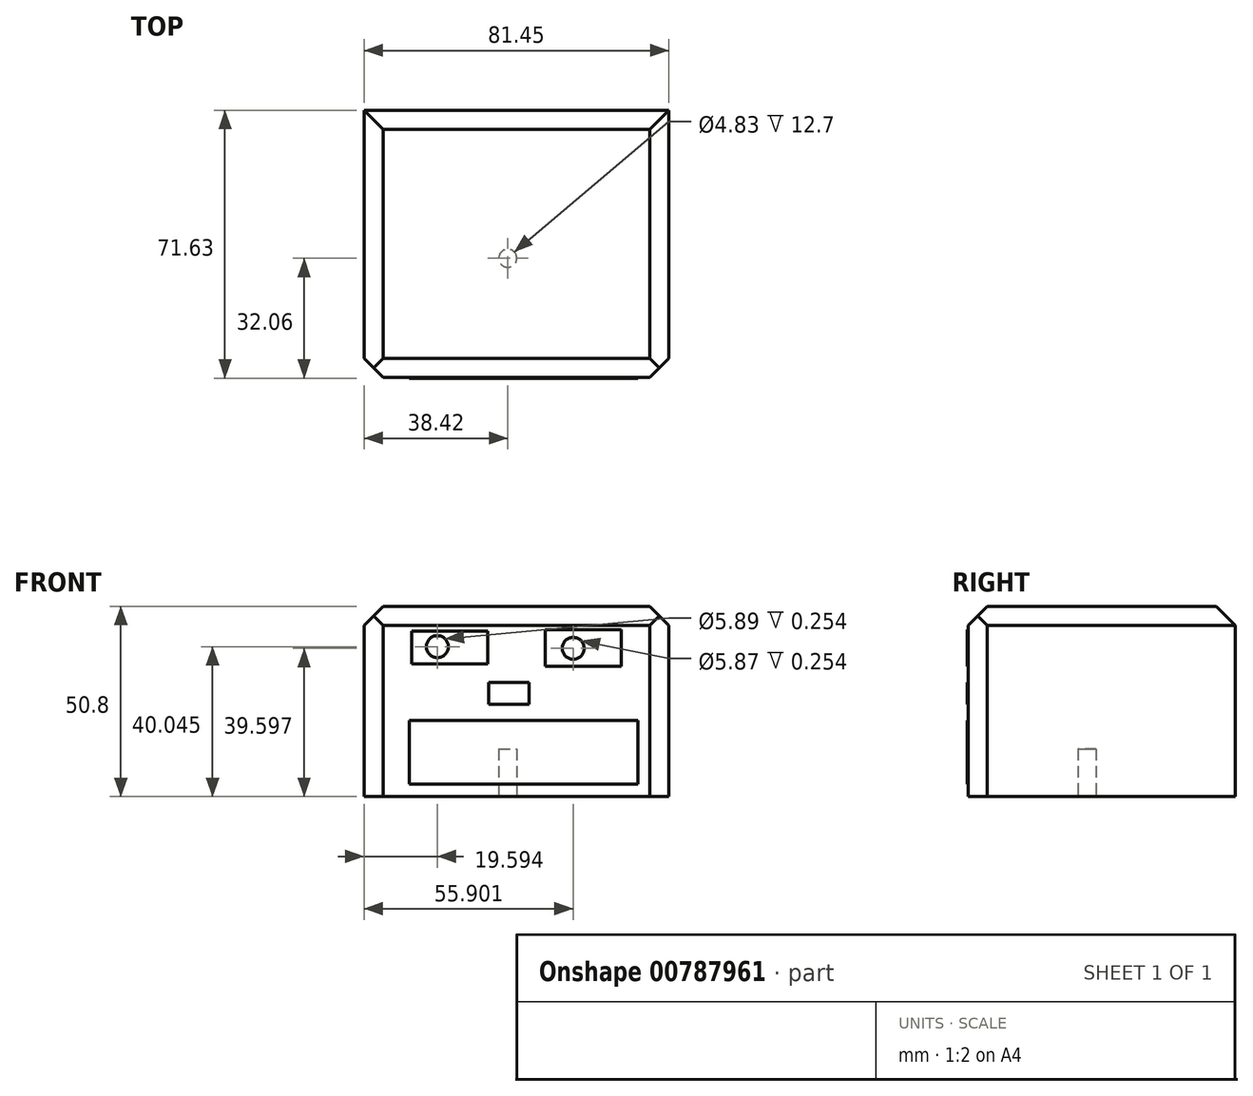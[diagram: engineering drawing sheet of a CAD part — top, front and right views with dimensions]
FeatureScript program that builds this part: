
annotation { "Feature Type Name" : "Feature", "Feature Type Description" : "" }
export const myFeature = defineFeature(function(context is Context, id is Id, definition is map)
    precondition{}
    {
        {
            var Q0;
            Q0=qCreatedBy(makeId("Top.planeOp"),FACE);
            var sketch = newSketch(context, id + "F0", { "sketchPlane" : qUnion([Q0])});
            skLineSegment(sketch, "E0.bottom", {"start": v(-38.42, 39.57) * mm, "end": v(43.03, 39.57) * mm});
            skLineSegment(sketch, "E0.top", {"start": v(-38.42, -31.8) * mm, "end": v(43.03, -31.8) * mm});
            skLineSegment(sketch, "E0.left", {"start": v(-38.42, 39.57) * mm, "end": v(-38.42, -31.8) * mm});
            skLineSegment(sketch, "E0.right", {"start": v(43.03, 39.57) * mm, "end": v(43.03, -31.8) * mm});
            skSolve(sketch);
        }
        {
            var Q0;
            Q0 = qSketchRegion(id + "F0", true);
            extrude(context, id + "F1", {"entities" : qUnion([Q0]), "depth" : 50.8 * mm, "offsetDistance" : 25.4 * mm});
        }
        {
            var Q0;
            Q0=makeQuery(id+"F1.opExtrude","SWEPT_FACE",FACE,{"disambiguationData":[OSD([sQuery(id+"F0.wireOp",EDGE,"E0.top")])]});
            var sketch = newSketch(context, id + "F2", { "sketchPlane" : qUnion([Q0])});
            skLineSegment(sketch, "E1.bottom", {"start": v(-25.72, 44.23) * mm, "end": v(-5.4, 44.23) * mm});
            skLineSegment(sketch, "E1.top", {"start": v(-25.72, 35.41) * mm, "end": v(-5.4, 35.41) * mm});
            skLineSegment(sketch, "E1.left", {"start": v(-25.72, 44.23) * mm, "end": v(-25.72, 35.41) * mm});
            skLineSegment(sketch, "E1.right", {"start": v(-5.4, 44.23) * mm, "end": v(-5.4, 35.41) * mm});
            skLineSegment(sketch, "E2.bottom", {"start": v(10, 44.52) * mm, "end": v(30.33, 44.52) * mm});
            skLineSegment(sketch, "E2.top", {"start": v(10, 34.81) * mm, "end": v(30.33, 34.81) * mm});
            skLineSegment(sketch, "E2.left", {"start": v(10, 44.52) * mm, "end": v(10, 34.81) * mm});
            skLineSegment(sketch, "E2.right", {"start": v(30.33, 44.52) * mm, "end": v(30.33, 34.81) * mm});
            skLineSegment(sketch, "E3.bottom", {"start": v(-5.08, 30.48) * mm, "end": v(5.68, 30.48) * mm});
            skLineSegment(sketch, "E3.top", {"start": v(-5.08, 24.65) * mm, "end": v(5.68, 24.65) * mm});
            skLineSegment(sketch, "E3.left", {"start": v(-5.08, 30.48) * mm, "end": v(-5.08, 24.65) * mm});
            skLineSegment(sketch, "E3.right", {"start": v(5.68, 30.48) * mm, "end": v(5.68, 24.65) * mm});
            skLineSegment(sketch, "E4.bottom", {"start": v(-26.3, 20.32) * mm, "end": v(34.81, 20.32) * mm});
            skLineSegment(sketch, "E4.top", {"start": v(-26.3, 3.29) * mm, "end": v(34.81, 3.29) * mm});
            skLineSegment(sketch, "E4.left", {"start": v(-26.3, 20.32) * mm, "end": v(-26.3, 3.29) * mm});
            skLineSegment(sketch, "E4.right", {"start": v(34.81, 20.32) * mm, "end": v(34.81, 3.29) * mm});
            skLineSegment(sketch, "E5", {"start": v(-26.3, 20.32) * mm, "end": v(-22.11, 16.58) * mm});
            skLineSegment(sketch, "E6", {"start": v(-22.11, 16.58) * mm, "end": v(-16.88, 20.32) * mm});
            skLineSegment(sketch, "E7", {"start": v(-16.88, 20.32) * mm, "end": v(-14.22, 16.58) * mm});
            skLineSegment(sketch, "E8", {"start": v(-14.22, 16.58) * mm, "end": v(-8.99, 20.32) * mm});
            skLineSegment(sketch, "E9", {"start": v(-8.99, 20.32) * mm, "end": v(-4.63, 16.58) * mm});
            skLineSegment(sketch, "E10", {"start": v(-4.63, 16.58) * mm, "end": v(-1.43, 20.32) * mm});
            skLineSegment(sketch, "E11", {"start": v(-1.43, 20.32) * mm, "end": v(2.93, 16.58) * mm});
            skLineSegment(sketch, "E12", {"start": v(2.93, 16.58) * mm, "end": v(4.26, 20.32) * mm});
            skLineSegment(sketch, "E13", {"start": v(4.26, 20.32) * mm, "end": v(8.82, 16.58) * mm});
            skLineSegment(sketch, "E14", {"start": v(8.82, 16.58) * mm, "end": v(11.88, 20.32) * mm});
            skLineSegment(sketch, "E15", {"start": v(11.88, 20.32) * mm, "end": v(16.43, 16.58) * mm});
            skLineSegment(sketch, "E16", {"start": v(16.43, 16.58) * mm, "end": v(19.5, 20.32) * mm});
            skLineSegment(sketch, "E17", {"start": v(19.5, 20.32) * mm, "end": v(24.05, 16.58) * mm});
            skLineSegment(sketch, "E18", {"start": v(24.05, 16.58) * mm, "end": v(25.25, 20.32) * mm});
            skLineSegment(sketch, "E19", {"start": v(25.25, 20.32) * mm, "end": v(29.14, 16.58) * mm});
            skLineSegment(sketch, "E20", {"start": v(29.14, 16.58) * mm, "end": v(30.93, 20.32) * mm});
            skLineSegment(sketch, "E21", {"start": v(30.93, 20.32) * mm, "end": v(34.81, 15.39) * mm});
            skLineSegment(sketch, "E22", {"start": v(-26.3, 3.29) * mm, "end": v(-22.88, 7.27) * mm});
            skLineSegment(sketch, "E23", {"start": v(-22.88, 7.27) * mm, "end": v(-18.23, 3.29) * mm});
            skLineSegment(sketch, "E24", {"start": v(-18.23, 3.29) * mm, "end": v(-15.54, 8.52) * mm});
            skLineSegment(sketch, "E25", {"start": v(-15.54, 8.52) * mm, "end": v(-11.5, 3.29) * mm});
            skLineSegment(sketch, "E26", {"start": v(-11.5, 3.29) * mm, "end": v(-9.26, 8.67) * mm});
            skLineSegment(sketch, "E27", {"start": v(-9.26, 8.67) * mm, "end": v(-6.13, 3.29) * mm});
            skLineSegment(sketch, "E28", {"start": v(-6.13, 3.29) * mm, "end": v(-4.63, 8.22) * mm});
            skLineSegment(sketch, "E29", {"start": v(-4.63, 8.22) * mm, "end": v(0, 4.24) * mm});
            skLineSegment(sketch, "E30", {"start": v(0, 4.24) * mm, "end": v(1.64, 8.37) * mm});
            skLineSegment(sketch, "E31", {"start": v(1.64, 8.37) * mm, "end": v(6.13, 3.29) * mm});
            skLineSegment(sketch, "E32", {"start": v(6.13, 3.29) * mm, "end": v(10.34, 8.2) * mm});
            skLineSegment(sketch, "E33", {"start": v(10.34, 8.2) * mm, "end": v(12.85, 3.29) * mm});
            skLineSegment(sketch, "E34", {"start": v(12.85, 3.29) * mm, "end": v(17.05, 8.18) * mm});
            skLineSegment(sketch, "E35", {"start": v(17.05, 8.18) * mm, "end": v(21.07, 3.29) * mm});
            skLineSegment(sketch, "E36", {"start": v(21.07, 3.29) * mm, "end": v(22.71, 8.67) * mm});
            skLineSegment(sketch, "E37", {"start": v(22.71, 8.67) * mm, "end": v(26.74, 3.29) * mm});
            skLineSegment(sketch, "E38", {"start": v(26.74, 3.29) * mm, "end": v(28.69, 9.26) * mm});
            skLineSegment(sketch, "E39", {"start": v(28.69, 9.26) * mm, "end": v(32.87, 3.29) * mm});
            skLineSegment(sketch, "E40", {"start": v(32.87, 3.29) * mm, "end": v(34.81, 10.3) * mm});
            skCircle(sketch, "E41", {"center": v(-18.83, 40.04) * mm, "radius": 2.95 * mm});
            skCircle(sketch, "E42", {"center": v(17.48, 39.6) * mm, "radius": 2.94 * mm});
            skArc(sketch, "E43", {"start": v(-8.96, 47.22) * mm, "mid": v(-18.06, 50.23) * mm, "end": v(-27.04, 46.92) * mm});
            skArc(sketch, "E44", {"start": v(29.14, 47.82) * mm, "mid": v(18.6, 50.63) * mm, "end": v(8.07, 47.82) * mm});
            skSolve(sketch);
        }
        {
            var Q0;
            Q0 = qSketchRegion(id + "F2", true);
            extrude(context, id + "F3", {"entities" : qUnion([Q0]), "operationType" : NewBodyOperationType.ADD, "depth" : 0.25 * mm, "offsetDistance" : 25.4 * mm});
        }
        {
            var Q0;
            Q0=makeQuery(id+"F1.opExtrude","CAP_EDGE",EDGE,{"disambiguationData":[OSD([sQuery(id+"F0.wireOp",EDGE,"E0.top")])],"isStart":false});
            var Q1;
            Q1=makeQuery(id+"F1.opExtrude","SWEPT_EDGE",EDGE,{"disambiguationData":[OSD([sQuery(id+"F0.wireOp",EDGE,"E0.top"),sQuery(id+"F0.wireOp",EDGE,"E0.left")])]});
            var Q2;
            Q2=makeQuery(id+"F1.opExtrude","SWEPT_EDGE",EDGE,{"disambiguationData":[OSD([sQuery(id+"F0.wireOp",EDGE,"E0.top"),sQuery(id+"F0.wireOp",EDGE,"E0.right")])]});
            chamfer(context, id + "F4", {"entities" : qUnion([Q0, Q1, Q2]), "width" : 5.08 * mm, "tangentPropagation" : true});
        }
        {
            var Q0;
            Q0=makeQuery(id+"F1.opExtrude","CAP_EDGE",EDGE,{"disambiguationData":[OSD([sQuery(id+"F0.wireOp",EDGE,"E0.left")])],"isStart":false});
            var Q1;
            Q1=makeQuery(id+"F1.opExtrude","CAP_EDGE",EDGE,{"disambiguationData":[OSD([sQuery(id+"F0.wireOp",EDGE,"E0.right")])],"isStart":false});
            var Q2;
            Q2=makeQuery(id+"F1.opExtrude","CAP_EDGE",EDGE,{"disambiguationData":[OSD([sQuery(id+"F0.wireOp",EDGE,"E0.bottom")])],"isStart":false});
            chamfer(context, id + "F5", {"entities" : qUnion([Q0, Q1, Q2]), "width" : 5.08 * mm, "tangentPropagation" : true});
        }
        {
            var Q0;
            Q0=makeQuery(id+"F1.opExtrude","CAP_FACE",FACE,{"disambiguationData":[OSD([sQuery(id+"F0.wireOp",EDGE,"E0.bottom"),sQuery(id+"F0.wireOp",EDGE,"E0.top"),sQuery(id+"F0.wireOp",EDGE,"E0.left"),sQuery(id+"F0.wireOp",EDGE,"E0.right")])],"isStart":true});
            var sketch = newSketch(context, id + "F6", { "sketchPlane" : qUnion([Q0])});
            skCircle(sketch, "E45", {"center": v(0, 0) * mm, "radius": 2.41 * mm});
            skSolve(sketch);
        }
        {
            var Q0;
            Q0 = qSketchRegion(id + "F6", true);
            extrude(context, id + "F7", {"entities" : qUnion([Q0]), "operationType" : NewBodyOperationType.REMOVE, "oppositeDirection" : true, "depth" : 12.7 * mm, "offsetDistance" : 25.4 * mm});
        }
    });
